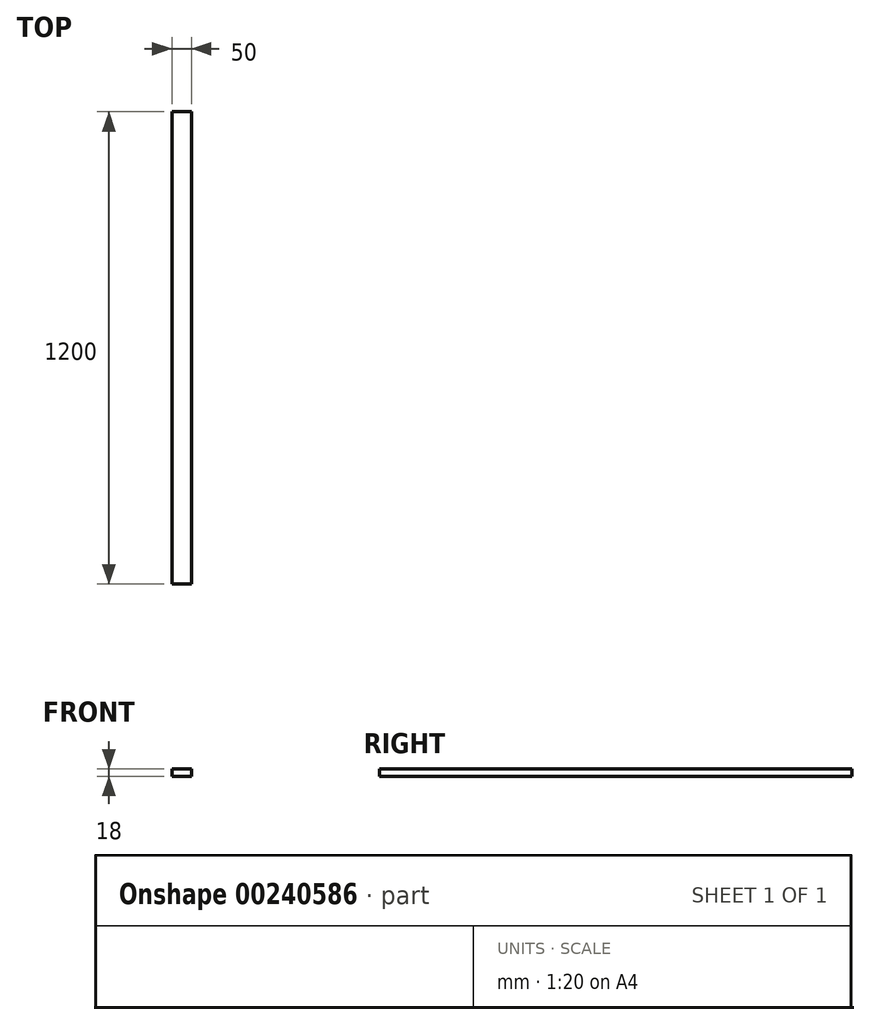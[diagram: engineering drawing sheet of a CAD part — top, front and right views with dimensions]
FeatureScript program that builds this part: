
annotation { "Feature Type Name" : "Feature", "Feature Type Description" : "" }
export const myFeature = defineFeature(function(context is Context, id is Id, definition is map)
    precondition{}
    {
        {
            var Q0;
            Q0=qCreatedBy(makeId("Top.planeOp"),FACE);
            var sketch = newSketch(context, id + "F0", { "sketchPlane" : qUnion([Q0])});
            skLineSegment(sketch, "E0.bottom", {"start": v(-11.09, 1098.07) * mm, "end": v(38.91, 1098.07) * mm});
            skLineSegment(sketch, "E0.top", {"start": v(-11.09, -101.93) * mm, "end": v(38.91, -101.93) * mm});
            skLineSegment(sketch, "E0.left", {"start": v(-11.09, 1098.07) * mm, "end": v(-11.09, -101.93) * mm});
            skLineSegment(sketch, "E0.right", {"start": v(38.91, 1098.07) * mm, "end": v(38.91, -101.93) * mm});
            skSolve(sketch);
        }
        {
            var Q0;
            Q0=makeQuery(id+"F0.imprint","IMPRINT",FACE,{"disambiguationData":[TD([[makeQuery(id+"F0.imprint","IMPRINT",EDGE,{"derivedFrom":sQuery(id+"F0.wireOp",EDGE,"E0.bottom")}),-1.0]])]});
            extrude(context, id + "F1", {"entities" : qUnion([Q0]), "depth" : 18 * mm});
        }
    });
